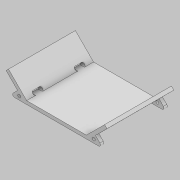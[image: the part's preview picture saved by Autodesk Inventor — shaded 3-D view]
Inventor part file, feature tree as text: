
AUTODESK INVENTOR PART (.ipt)
format: ipt  version: 2022.2 (Build 262287010, 287A)  size: 173,056 bytes
history: native  units: mm
features: extrude x4, sketch x3, other x1, plane x1, mirror x1, fillet x1
ambient origin geometry x8: Origin, YZ Plane, XZ Plane, XY Plane, X Axis, Y Axis, Z Axis, Center Point
bodies: Body1 (feature_tree)
feature tree (11):
  other  "Sólido1"
  extrude  "Extrusión1"  Depth=23.547982mm
  extrude  "Extrusión2"  Depth=3.5mm
  plane  "Plano de trabajo1"
  mirror  "Simetría1"
  extrude  "Extrusión3"  Depth=32.756mm
  fillet  "Empalme1"  Radius=70.0mm
  extrude  "Extrusión4"  Depth=3.5mm TaperAngle=0.0deg
  sketch  "Boceto1"  dims[d0=45.0deg d1=23.547982mm]
  sketch  "Boceto3"  dims[d2=3.5mm d3=3.5mm]
  sketch  "Boceto4"  dims[d4=28.326mm d5=32.756mm d6=70.0mm d7=0.0mm d10=3.5mm d11=0.0mm d12=16.0mm d13=3.0mm d14=7.1mm d15=1.738mm d16=0.0mm d17=0.0mm d18=2.0mm d19=10.0mm d20=3.0mm d21=8.0mm d22=0.0mm d23=0.0mm]
